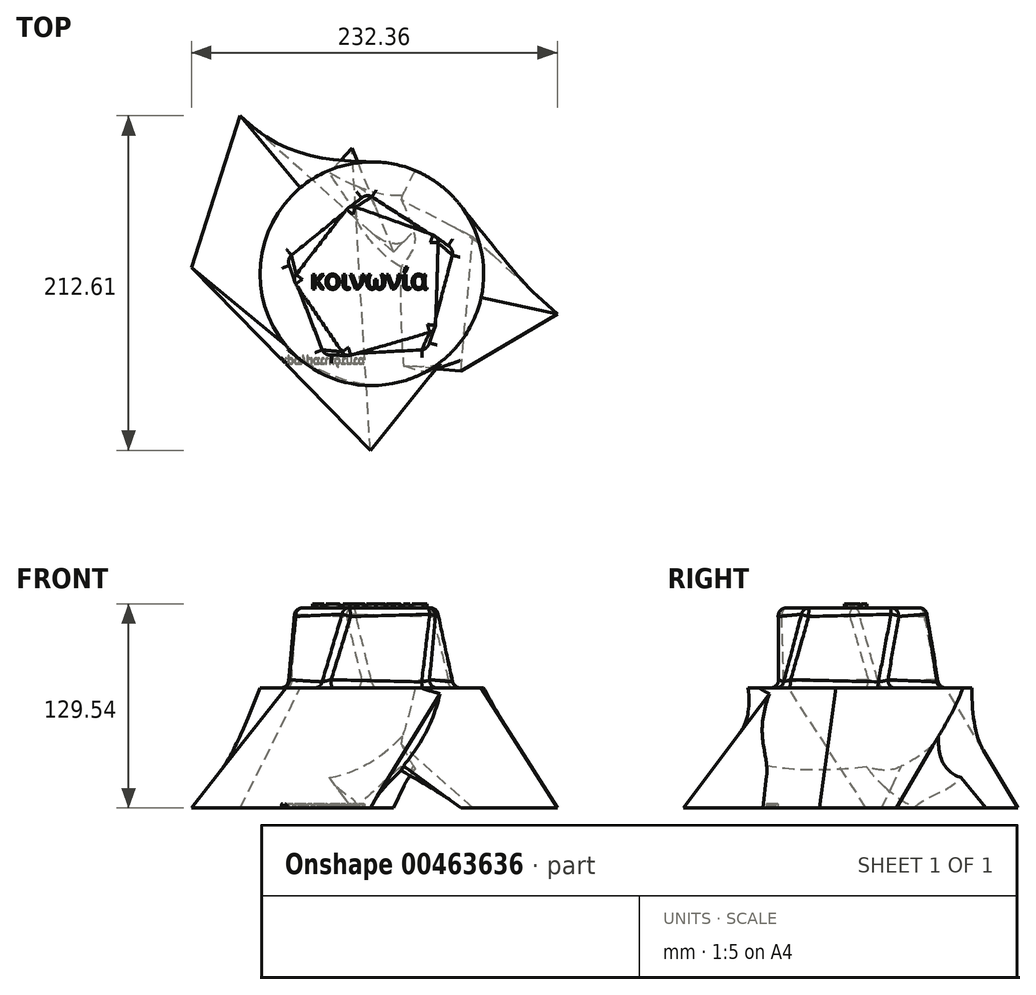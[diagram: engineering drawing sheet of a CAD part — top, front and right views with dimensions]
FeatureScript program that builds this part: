
annotation { "Feature Type Name" : "Feature", "Feature Type Description" : "" }
export const myFeature = defineFeature(function(context is Context, id is Id, definition is map)
    precondition{}
    {
        {
            var Q0;
            Q0=qCreatedBy(makeId("Top.planeOp"),FACE);
            var sketch = newSketch(context, id + "F0", { "sketchPlane" : qUnion([Q0])});
            skLineSegment(sketch, "E0", {"start": v(0, 0) * mm, "end": v(-97.26, 86.63) * mm});
            skLineSegment(sketch, "E1", {"start": v(-97.26, 86.63) * mm, "end": v(-128.27, -9.84) * mm});
            skLineSegment(sketch, "E2", {"start": v(-128.27, -9.84) * mm, "end": v(-14.65, -125.98) * mm});
            skLineSegment(sketch, "E3", {"start": v(-14.65, -125.98) * mm, "end": v(-27.26, 80.42) * mm});
            skLineSegment(sketch, "E4", {"start": v(-27.26, 80.42) * mm, "end": v(104.09, -39.43) * mm});
            skLineSegment(sketch, "E5", {"start": v(104.09, -39.43) * mm, "end": v(42.93, -75.44) * mm});
            skLineSegment(sketch, "E6", {"start": v(42.93, -75.44) * mm, "end": v(55.36, 65) * mm});
            skLineSegment(sketch, "E7", {"start": v(55.36, 65) * mm, "end": v(-98.76, 193.08) * mm});
            skLineSegment(sketch, "E8", {"start": v(-98.76, 193.08) * mm, "end": v(-139.74, 86.58) * mm});
            skLineSegment(sketch, "E9", {"start": v(-139.74, 86.58) * mm, "end": v(-50.24, 125.96) * mm});
            skLineSegment(sketch, "E10", {"start": v(-50.24, 125.96) * mm, "end": v(0, 0) * mm});
            skSolve(sketch);
        }
        {
            var Q0;
            Q0=qCreatedBy(makeId("Right.planeOp"),FACE);
            cPlane(context, id + "F1", {"entities" : qUnion([Q0]), "cplaneType" : CPlaneType.OFFSET, "offset" : 76.2 * mm, "oppositeDirection" : true, "width" : 152.4 * mm, "height" : 152.4 * mm});
        }
        {
            var Q0;
            Q0=qCreatedBy(makeId("Top.planeOp"),FACE);
            cPlane(context, id + "F2", {"entities" : qUnion([Q0]), "cplaneType" : CPlaneType.OFFSET, "offset" : 76.2 * mm, "width" : 152.4 * mm, "height" : 152.4 * mm});
        }
        {
            var Q0;
            Q0=qCreatedBy(id+"F2.planeOp",FACE);
            var sketch = newSketch(context, id + "F3", { "sketchPlane" : qUnion([Q0])});
            skCircle(sketch, "E11", {"center": v(-13.7, -13.77) * mm, "radius": 71.06 * mm});
            skSolve(sketch);
        }
        {
            var Q0;
            {var subQ0=sQuery(id+"F0.wireOp",EDGE,"E5");Q0=makeQuery(id+"F0.imprint","IMPRINT",FACE,{"disambiguationData":[TD([[makeQuery(id+"F0.imprint","IMPRINT",EDGE,{"derivedFrom":subQ0}),-1.0]])]});}
            var Q1;
            Q1=makeQuery(id+"F3.imprint","IMPRINT",FACE,{"disambiguationData":[TD([[makeQuery(id+"F3.imprint","IMPRINT",EDGE,{"derivedFrom":sQuery(id+"F3.wireOp",EDGE,"E11")}),1.0]])]});
            loft(context, id + "F4", {"sheetProfilesArray" : [{ "sheetProfileEntities" : qUnion([Q0]) }, { "sheetProfileEntities" : qUnion([Q1]) }]});
        }
        {
            var Q1;
            {var subQ0=sQuery(id+"F0.wireOp",EDGE,"E1");Q1=makeQuery(id+"F0.imprint","IMPRINT",FACE,{"disambiguationData":[TD([[makeQuery(id+"F0.imprint","IMPRINT",EDGE,{"derivedFrom":subQ0}),1.0]])]});}
            var Q2;
            Q2=makeQuery(id+"F3.imprint","IMPRINT",FACE,{"disambiguationData":[TD([[makeQuery(id+"F3.imprint","IMPRINT",EDGE,{"derivedFrom":sQuery(id+"F3.wireOp",EDGE,"E11")}),1.0]])]});
            loft(context, id + "F5", {"operationType" : NewBodyOperationType.ADD, "sheetProfilesArray" : [{ "sheetProfileEntities" : qUnion([Q1]) }, { "sheetProfileEntities" : qUnion([Q2]) }]});
        }
        {
            var Q1;
            {var subQ0=sQuery(id+"F0.wireOp",EDGE,"E10");var subQ1=sQuery(id+"F0.wireOp",EDGE,"E0");var subQ2=makeQuery(id+"F0.imprint","INTERSECT",VERTEX,{"derivedFrom":[subQ1,subQ0]});Q1=makeQuery(id+"F0.imprint","IMPRINT",FACE,{"disambiguationData":[TD([[makeQuery(id+"F0.imprint","IMPRINT",EDGE,{"disambiguationData":[TD([[subQ2,-1.0]])],"derivedFrom":subQ1}),-1.0]])]});}
            var Q2;
            Q2=makeQuery(id+"F3.imprint","IMPRINT",FACE,{"disambiguationData":[TD([[makeQuery(id+"F3.imprint","IMPRINT",EDGE,{"derivedFrom":sQuery(id+"F3.wireOp",EDGE,"E11")}),1.0]])]});
            loft(context, id + "F6", {"operationType" : NewBodyOperationType.ADD, "sheetProfilesArray" : [{ "sheetProfileEntities" : qUnion([Q1]) }, { "sheetProfileEntities" : qUnion([Q2]) }]});
        }
        {
            var Q0;
            Q0=makeQuery(id+"F3.imprint","IMPRINT",FACE,{"disambiguationData":[TD([[makeQuery(id+"F3.imprint","IMPRINT",EDGE,{"derivedFrom":sQuery(id+"F3.wireOp",EDGE,"E11")}),1.0]])]});
            var sketch = newSketch(context, id + "F7", { "sketchPlane" : qUnion([Q0])});
            skCircle(sketch, "E12.cCircle", {"center": v(-13.65, -18.64) * mm, "radius": 56.48 * mm, "construction": true});
            skLineSegment(sketch, "E12.0", {"start": v(21.31, -63) * mm, "end": v(-45.03, -65.6) * mm});
            skLineSegment(sketch, "E12.1", {"start": v(-45.03, -65.6) * mm, "end": v(-68, -3.3) * mm});
            skLineSegment(sketch, "E12.2", {"start": v(-68, -3.3) * mm, "end": v(-15.86, 37.8) * mm});
            skLineSegment(sketch, "E12.3", {"start": v(-15.86, 37.8) * mm, "end": v(39.34, 0.9) * mm});
            skLineSegment(sketch, "E12.4", {"start": v(39.34, 0.9) * mm, "end": v(21.31, -63) * mm});
            skSolve(sketch);
        }
        {
            var Q0;
            Q0=qCreatedBy(makeId("Top.planeOp"),FACE);
            cPlane(context, id + "F8", {"entities" : qUnion([Q0]), "cplaneType" : CPlaneType.OFFSET, "offset" : 127 * mm, "width" : 152.4 * mm, "height" : 152.4 * mm});
        }
        {
            var Q0;
            Q0=qCreatedBy(id+"F8.planeOp",FACE);
            var sketch = newSketch(context, id + "F9", { "sketchPlane" : qUnion([Q0])});
            skCircle(sketch, "E13.cCircle", {"center": v(-13.38, -18.83) * mm, "radius": 50.39 * mm, "construction": true});
            skLineSegment(sketch, "E13.0", {"start": v(27.21, -48.69) * mm, "end": v(-29.23, -66.66) * mm});
            skLineSegment(sketch, "E13.1", {"start": v(-29.23, -66.66) * mm, "end": v(-63.76, -18.54) * mm});
            skLineSegment(sketch, "E13.2", {"start": v(-63.76, -18.54) * mm, "end": v(-28.67, 29.18) * mm});
            skLineSegment(sketch, "E13.3", {"start": v(-28.67, 29.18) * mm, "end": v(27.56, 10.55) * mm});
            skLineSegment(sketch, "E13.4", {"start": v(27.56, 10.55) * mm, "end": v(27.21, -48.69) * mm});
            skSolve(sketch);
        }
        {
            var Q1;
            Q1=makeQuery(id+"F7.imprint","IMPRINT",FACE,{"disambiguationData":[TD([[makeQuery(id+"F7.imprint","IMPRINT",EDGE,{"derivedFrom":sQuery(id+"F7.wireOp",EDGE,"E12.0")}),-1.0]])]});
            var Q2;
            Q2=makeQuery(id+"F9.imprint","IMPRINT",FACE,{"disambiguationData":[TD([[makeQuery(id+"F9.imprint","IMPRINT",EDGE,{"derivedFrom":sQuery(id+"F9.wireOp",EDGE,"E13.0")}),-1.0]])]});
            loft(context, id + "F10", {"operationType" : NewBodyOperationType.ADD, "sheetProfilesArray" : [{ "sheetProfileEntities" : qUnion([Q1]) }, { "sheetProfileEntities" : qUnion([Q2]) }]});
        }
        {
            var Q0;
            Q0=makeQuery(id+"F10.opLoft","SWEPT_FACE",FACE,{"disambiguationData":[OSD([sQuery(id+"F7.wireOp",EDGE,"E12.2"),sQuery(id+"F7.wireOp",EDGE,"E12.3"),sQuery(id+"F7.wireOp",EDGE,"E12.4"),sQuery(id+"F9.wireOp",EDGE,"E13.2"),sQuery(id+"F9.wireOp",EDGE,"E13.3"),sQuery(id+"F9.wireOp",EDGE,"E13.4")])]});
            var Q1;
            Q1=makeQuery(id+"F10.opLoft","SWEPT_FACE",FACE,{"disambiguationData":[OSD([sQuery(id+"F7.wireOp",EDGE,"E12.1"),sQuery(id+"F7.wireOp",EDGE,"E12.2"),sQuery(id+"F7.wireOp",EDGE,"E12.3"),sQuery(id+"F9.wireOp",EDGE,"E13.1"),sQuery(id+"F9.wireOp",EDGE,"E13.2"),sQuery(id+"F9.wireOp",EDGE,"E13.3")])]});
            var Q2;
            Q2=makeQuery(id+"F10.opLoft","SWEPT_FACE",FACE,{"disambiguationData":[OSD([sQuery(id+"F7.wireOp",EDGE,"E12.0"),sQuery(id+"F7.wireOp",EDGE,"E12.1"),sQuery(id+"F7.wireOp",EDGE,"E12.2"),sQuery(id+"F9.wireOp",EDGE,"E13.0"),sQuery(id+"F9.wireOp",EDGE,"E13.1"),sQuery(id+"F9.wireOp",EDGE,"E13.2")])]});
            var Q3;
            Q3=makeQuery(id+"F10.opLoft","SWEPT_FACE",FACE,{"disambiguationData":[OSD([sQuery(id+"F7.wireOp",EDGE,"E12.0"),sQuery(id+"F7.wireOp",EDGE,"E12.1"),sQuery(id+"F7.wireOp",EDGE,"E12.4"),sQuery(id+"F9.wireOp",EDGE,"E13.0"),sQuery(id+"F9.wireOp",EDGE,"E13.1"),sQuery(id+"F9.wireOp",EDGE,"E13.4")])]});
            var Q4;
            Q4=makeQuery(id+"F10.opLoft","SWEPT_FACE",FACE,{"disambiguationData":[OSD([sQuery(id+"F7.wireOp",EDGE,"E12.0"),sQuery(id+"F7.wireOp",EDGE,"E12.3"),sQuery(id+"F7.wireOp",EDGE,"E12.4"),sQuery(id+"F9.wireOp",EDGE,"E13.0"),sQuery(id+"F9.wireOp",EDGE,"E13.3"),sQuery(id+"F9.wireOp",EDGE,"E13.4")])]});
            fillet(context, id + "F11", {"entities" : qUnion([Q0, Q1, Q2, Q3, Q4]), "radius" : 5.08 * mm, "tangentPropagation" : true, "allowEdgeOverflow" : false});
        }
        {
            var Q0;
            Q0=makeQuery(id+"F10.opLoft","CAP_FACE",FACE,{"disambiguationData":[OSD([makeQuery(id+"F9.imprint","IMPRINT",FACE,{"disambiguationData":[TD([[makeQuery(id+"F9.imprint","IMPRINT",EDGE,{"derivedFrom":sQuery(id+"F9.wireOp",EDGE,"E13.0")}),-1.0]])]})])],"isStart":true});
            var sketch = newSketch(context, id + "F12", { "sketchPlane" : qUnion([Q0])});
            skText(sketch, "E14", { "text": "κοινωνία", "fontName": "OpenSans-Regular.ttf"});
            const initialGuessF12  = {"E14": [-0.0529, -0.02354, 1, 0, 0.01257]};
            skSetInitialGuess(sketch, initialGuessF12);
            skSolve(sketch);
        }
        {
            var Q0;
            Q0 = qSketchRegion(id + "F12", true);
            extrude(context, id + "F13", {"entities" : qUnion([Q0]), "operationType" : NewBodyOperationType.ADD, "depth" : 2.54 * mm});
        }
        {
            var Q0;
            {var subQ0=sQuery(id+"F0.wireOp",EDGE,"E1");Q0=makeQuery(id+"F5.opLoft","CAP_FACE",FACE,{"disambiguationData":[OSD([makeQuery(id+"F0.imprint","IMPRINT",FACE,{"disambiguationData":[TD([[makeQuery(id+"F0.imprint","IMPRINT",EDGE,{"derivedFrom":subQ0}),1.0]])]})])],"isStart":true});}
            var sketch = newSketch(context, id + "F14", { "sketchPlane" : qUnion([Q0])});
            skText(sketch, "E15", { "text": "πραγματικότητα", "fontName": "OpenSans-Regular.ttf"});
            const initialGuessF14  = {"E15": [-0.07193, 0.06743, 1, 0, 0.005]};
            skSetInitialGuess(sketch, initialGuessF14);
            skSolve(sketch);
        }
        {
            var Q0;
            Q0 = qSketchRegion(id + "F14", true);
            extrude(context, id + "F15", {"entities" : qUnion([Q0]), "operationType" : NewBodyOperationType.REMOVE, "oppositeDirection" : true, "depth" : 2.54 * mm});
        }
    });
